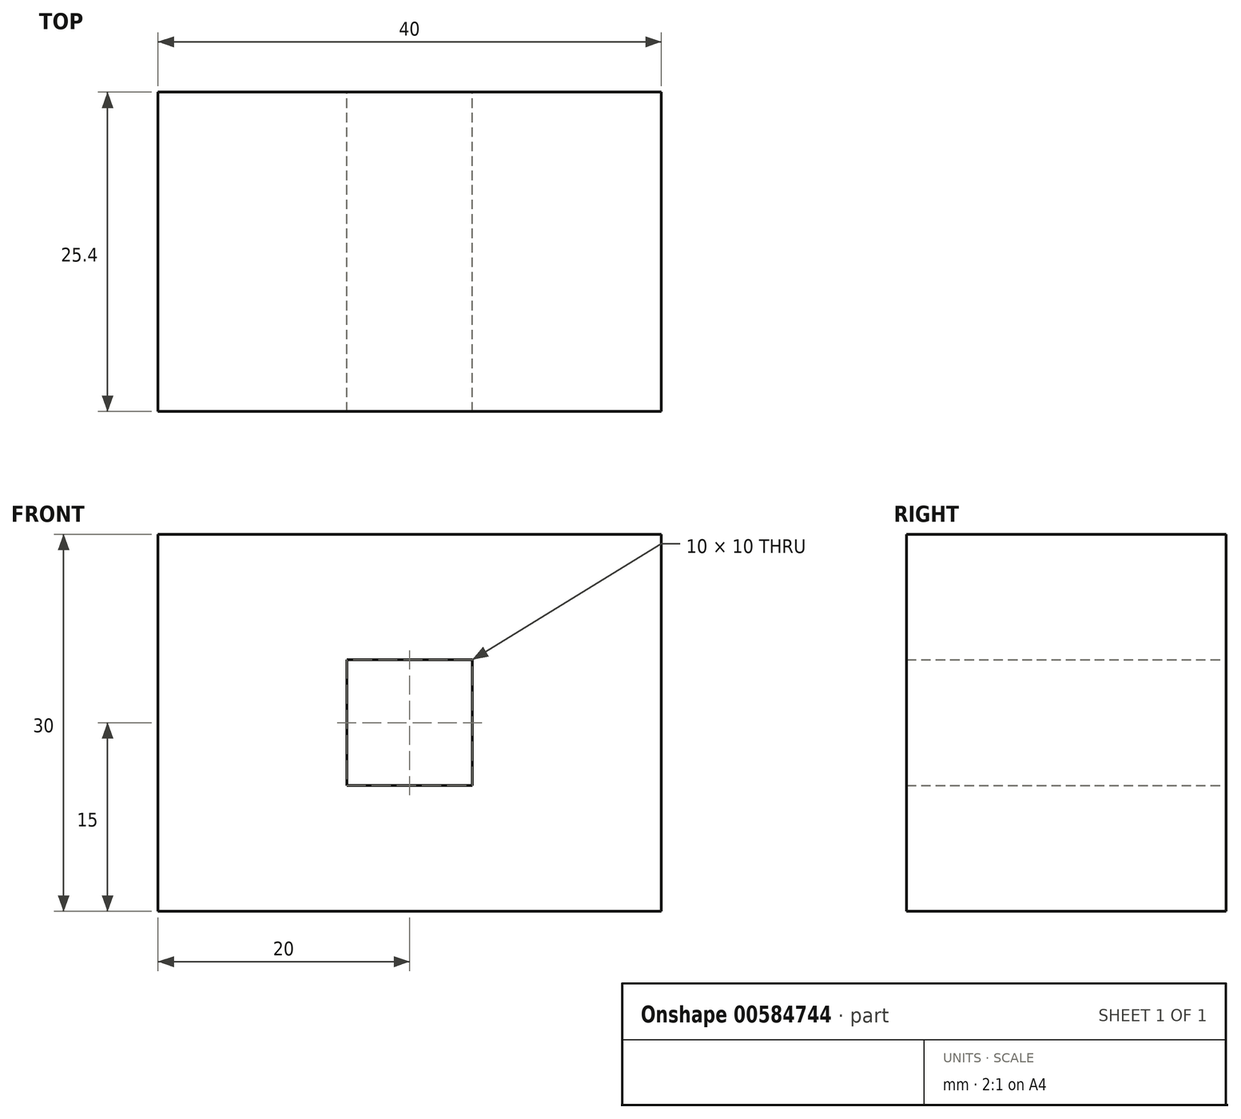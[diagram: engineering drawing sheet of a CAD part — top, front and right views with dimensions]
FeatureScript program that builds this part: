
annotation { "Feature Type Name" : "Feature", "Feature Type Description" : "" }
export const myFeature = defineFeature(function(context is Context, id is Id, definition is map)
    precondition{}
    {
        {
            var Q0;
            Q0=qCreatedBy(makeId("Front.planeOp"),FACE);
            var sketch = newSketch(context, id + "F0", { "sketchPlane" : qUnion([Q0])});
            skLineSegment(sketch, "E0.bottom", {"start": v(20, -15) * mm, "end": v(-20, -15) * mm});
            skLineSegment(sketch, "E0.top", {"start": v(20, 15) * mm, "end": v(-20, 15) * mm});
            skLineSegment(sketch, "E0.left", {"start": v(20, -15) * mm, "end": v(20, 15) * mm});
            skLineSegment(sketch, "E0.right", {"start": v(-20, -15) * mm, "end": v(-20, 15) * mm});
            skPoint(sketch, "E0.middle", {"position": v(0, 0) * mm});
            skSolve(sketch);
        }
        {
            var Q0;
            Q0=qCreatedBy(makeId("Front.planeOp"),FACE);
            var sketch = newSketch(context, id + "F1", { "sketchPlane" : qUnion([Q0])});
            skLineSegment(sketch, "E1.bottom", {"start": v(5, 5) * mm, "end": v(-5, 5) * mm});
            skLineSegment(sketch, "E1.top", {"start": v(5, -5) * mm, "end": v(-5, -5) * mm});
            skLineSegment(sketch, "E1.left", {"start": v(5, 5) * mm, "end": v(5, -5) * mm});
            skLineSegment(sketch, "E1.right", {"start": v(-5, 5) * mm, "end": v(-5, -5) * mm});
            skPoint(sketch, "E1.middle", {"position": v(0, 0) * mm});
            skSolve(sketch);
        }
        {
            var Q0;
            Q0 = qSketchRegion(id + "F0", true);
            extrude(context, id + "F2", {"entities" : qUnion([Q0]), "depth" : 25.4 * mm, "offsetDistance" : 25.4 * mm});
        }
        {
            var Q0;
            Q0 = qSketchRegion(id + "F1", true);
            extrude(context, id + "F3", {"entities" : qUnion([Q0]), "operationType" : NewBodyOperationType.REMOVE, "depth" : 63.75 * mm, "offsetDistance" : 25.4 * mm});
        }
    });
